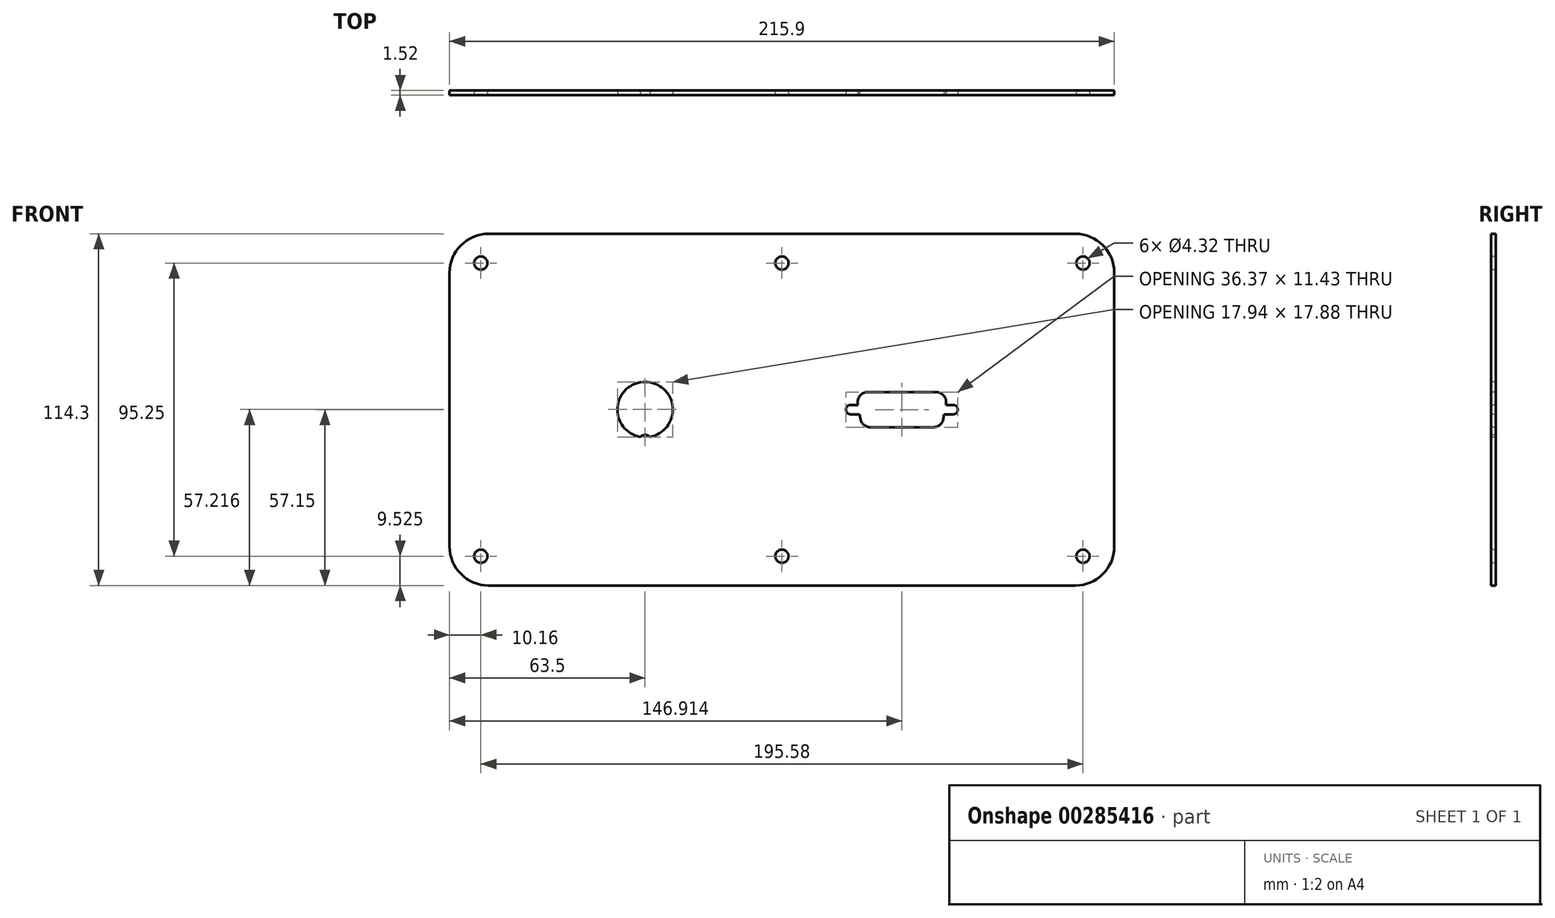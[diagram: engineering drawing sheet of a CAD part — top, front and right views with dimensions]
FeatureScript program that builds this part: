
annotation { "Feature Type Name" : "Feature", "Feature Type Description" : "" }
export const myFeature = defineFeature(function(context is Context, id is Id, definition is map)
    precondition{}
    {
        {
            var Q0;
            Q0=qCreatedBy(makeId("Front.planeOp"),FACE);
            var sketch = newSketch(context, id + "F0", { "sketchPlane" : qUnion([Q0])});
            skLineSegment(sketch, "E0.bottom", {"start": v(33.27, -22.23) * mm, "end": v(182.63, -22.23) * mm, "construction": true});
            skLineSegment(sketch, "E0.top", {"start": v(33.27, -92.08) * mm, "end": v(182.63, -92.08) * mm, "construction": true});
            skLineSegment(sketch, "E0.left", {"start": v(24.13, -31.37) * mm, "end": v(24.13, -82.93) * mm, "construction": true});
            skLineSegment(sketch, "E0.right", {"start": v(191.77, -31.37) * mm, "end": v(191.77, -82.93) * mm, "construction": true});
            skPoint(sketch, "E1.visualSharp", {"position": v(24.13, -22.23) * mm});
            skArc(sketch, "E1.filletArc", {"start": v(33.27, -22.23) * mm, "mid": v(26.8, -24.9) * mm, "end": v(24.13, -31.37) * mm, "construction": true});
            skPoint(sketch, "E2.visualSharp", {"position": v(191.77, -22.23) * mm});
            skArc(sketch, "E2.filletArc", {"start": v(191.77, -31.37) * mm, "mid": v(189.1, -24.9) * mm, "end": v(182.63, -22.22) * mm, "construction": true});
            skPoint(sketch, "E3.visualSharp", {"position": v(191.77, -92.08) * mm});
            skArc(sketch, "E3.filletArc", {"start": v(182.63, -92.08) * mm, "mid": v(189.1, -89.4) * mm, "end": v(191.77, -82.93) * mm, "construction": true});
            skPoint(sketch, "E4.visualSharp", {"position": v(24.13, -92.08) * mm});
            skArc(sketch, "E4.filletArc", {"start": v(24.13, -82.93) * mm, "mid": v(26.8, -89.4) * mm, "end": v(33.27, -92.07) * mm, "construction": true});
            skLineSegment(sketch, "E5.bottom", {"start": v(12.7, 0) * mm, "end": v(203.2, 0) * mm});
            skLineSegment(sketch, "E5.top", {"start": v(12.7, -114.3) * mm, "end": v(203.2, -114.3) * mm});
            skLineSegment(sketch, "E5.left", {"start": v(0, -12.7) * mm, "end": v(0, -101.6) * mm});
            skLineSegment(sketch, "E5.right", {"start": v(215.9, -12.7) * mm, "end": v(215.9, -101.6) * mm});
            skPoint(sketch, "E6.visualSharp", {"position": v(0, 0) * mm});
            skArc(sketch, "E6.filletArc", {"start": v(12.7, 0) * mm, "mid": v(3.72, -3.72) * mm, "end": v(0, -12.7) * mm});
            skPoint(sketch, "E7.visualSharp", {"position": v(215.9, 0) * mm});
            skArc(sketch, "E7.filletArc", {"start": v(215.9, -12.7) * mm, "mid": v(212.18, -3.72) * mm, "end": v(203.2, 0) * mm});
            skPoint(sketch, "E8.visualSharp", {"position": v(215.9, -114.3) * mm});
            skArc(sketch, "E8.filletArc", {"start": v(203.2, -114.3) * mm, "mid": v(212.18, -110.58) * mm, "end": v(215.9, -101.6) * mm});
            skPoint(sketch, "E9.visualSharp", {"position": v(0, -114.3) * mm});
            skArc(sketch, "E9.filletArc", {"start": v(0, -101.6) * mm, "mid": v(3.72, -110.58) * mm, "end": v(12.7, -114.3) * mm});
            skLineSegment(sketch, "E10", {"start": v(107.95, 0) * mm, "end": v(107.95, -114.3) * mm, "construction": true});
            skLineSegment(sketch, "E11", {"start": v(0, -57.15) * mm, "end": v(215.9, -57.15) * mm, "construction": true});
            skPoint(sketch, "E12", {"position": v(107.95, -22.23) * mm});
            skPoint(sketch, "E13", {"position": v(191.77, -57.15) * mm});
            skPoint(sketch, "E14", {"position": v(10.16, -9.52) * mm});
            skPoint(sketch, "E15", {"position": v(107.95, -9.52) * mm});
            skPoint(sketch, "E16", {"position": v(205.74, -9.52) * mm});
            skPoint(sketch, "E17", {"position": v(205.74, -104.78) * mm});
            skPoint(sketch, "E18", {"position": v(107.95, -104.78) * mm});
            skPoint(sketch, "E19", {"position": v(10.16, -104.78) * mm});
            skLineSegment(sketch, "E20", {"start": v(10.16, -9.52) * mm, "end": v(10.16, -104.78) * mm, "construction": true});
            skSolve(sketch);
        }
        {
            var Q0;
            Q0=makeQuery(id+"F0.imprint","IMPRINT",FACE,{"disambiguationData":[TD([[makeQuery(id+"F0.imprint","IMPRINT",EDGE,{"derivedFrom":sQuery(id+"F0.wireOp",EDGE,"E5.bottom")}),-1.0]])]});
            extrude(context, id + "F1", {"entities" : qUnion([Q0]), "depth" : 1.52 * mm});
        }
        {
            var Q0;
            Q0=makeQuery(id+"F1.opExtrude","CAP_FACE",FACE,{"disambiguationData":[OSD([sQuery(id+"F0.wireOp",EDGE,"E5.bottom"),sQuery(id+"F0.wireOp",EDGE,"E5.top"),sQuery(id+"F0.wireOp",EDGE,"E5.left"),sQuery(id+"F0.wireOp",EDGE,"E5.right"),sQuery(id+"F0.wireOp",EDGE,"E6.filletArc"),sQuery(id+"F0.wireOp",EDGE,"E7.filletArc"),sQuery(id+"F0.wireOp",EDGE,"E8.filletArc"),sQuery(id+"F0.wireOp",EDGE,"E9.filletArc")])],"isStart":false});
            var sketch = newSketch(context, id + "F2", { "sketchPlane" : qUnion([Q0])});
            skArc(sketch, "E21", {"start": v(65.04, -66.02) * mm, "mid": v(63.5, -48.15) * mm, "end": v(61.96, -66.02) * mm});
            skArc(sketch, "E22", {"start": v(65.04, -66.02) * mm, "mid": v(63.5, -65.35) * mm, "end": v(61.96, -66.02) * mm});
            skLineSegment(sketch, "E23", {"start": v(63.5, -57.15) * mm, "end": v(63.5, -65.35) * mm, "construction": true});
            skLineSegment(sketch, "E24", {"start": v(0, -57.15) * mm, "end": v(215.9, -57.15) * mm, "construction": true});
            skLineSegment(sketch, "E25.bottom", {"start": v(163.58, -51.44) * mm, "end": v(130.25, -51.44) * mm, "construction": true});
            skLineSegment(sketch, "E25.top", {"start": v(163.58, -62.87) * mm, "end": v(130.25, -62.87) * mm, "construction": true});
            skLineSegment(sketch, "E25.left", {"start": v(163.58, -51.44) * mm, "end": v(163.58, -62.87) * mm, "construction": true});
            skLineSegment(sketch, "E25.right", {"start": v(130.25, -51.44) * mm, "end": v(130.25, -62.87) * mm, "construction": true});
            skLineSegment(sketch, "E26", {"start": v(160.39, -60.14) * mm, "end": v(160.65, -58.67) * mm});
            skLineSegment(sketch, "E27", {"start": v(133.44, -60.14) * mm, "end": v(133.18, -58.67) * mm});
            skLineSegment(sketch, "E28", {"start": v(146.91, -62.87) * mm, "end": v(146.91, -51.44) * mm, "construction": true});
            skArc(sketch, "E29", {"start": v(163.58, -58.67) * mm, "mid": v(165.1, -57.15) * mm, "end": v(163.58, -55.63) * mm});
            skArc(sketch, "E30", {"start": v(130.25, -55.63) * mm, "mid": v(128.73, -57.15) * mm, "end": v(130.25, -58.67) * mm});
            skLineSegment(sketch, "E31", {"start": v(163.58, -57.15) * mm, "end": v(130.25, -57.15) * mm, "construction": true});
            skLineSegment(sketch, "E32", {"start": v(157.14, -62.87) * mm, "end": v(136.7, -62.87) * mm});
            skLineSegment(sketch, "E33", {"start": v(135.84, -51.44) * mm, "end": v(157.99, -51.44) * mm});
            skPoint(sketch, "E34.visualSharp", {"position": v(159.9, -62.87) * mm});
            skArc(sketch, "E34.filletArc", {"start": v(157.14, -62.87) * mm, "mid": v(159.26, -62.1) * mm, "end": v(160.39, -60.14) * mm});
            skPoint(sketch, "E35.visualSharp", {"position": v(133.92, -62.87) * mm});
            skArc(sketch, "E35.filletArc", {"start": v(133.44, -60.14) * mm, "mid": v(134.57, -62.1) * mm, "end": v(136.7, -62.87) * mm});
            skPoint(sketch, "E36.visualSharp", {"position": v(131.9, -51.44) * mm});
            skArc(sketch, "E36.filletArc", {"start": v(135.84, -51.44) * mm, "mid": v(133.3, -52.61) * mm, "end": v(132.59, -55.31) * mm});
            skPoint(sketch, "E37.visualSharp", {"position": v(161.92, -51.44) * mm});
            skArc(sketch, "E37.filletArc", {"start": v(161.24, -55.31) * mm, "mid": v(160.52, -52.61) * mm, "end": v(157.99, -51.44) * mm});
            skLineSegment(sketch, "E38", {"start": v(163.58, -58.67) * mm, "end": v(160.65, -58.67) * mm});
            skLineSegment(sketch, "E39", {"start": v(163.58, -55.63) * mm, "end": v(161.18, -55.63) * mm});
            skLineSegment(sketch, "E40", {"start": v(130.25, -58.67) * mm, "end": v(133.18, -58.67) * mm});
            skLineSegment(sketch, "E41", {"start": v(130.25, -55.63) * mm, "end": v(132.64, -55.63) * mm});
            skLineSegment(sketch, "E42.trimOffspring", {"start": v(132.64, -55.63) * mm, "end": v(132.59, -55.31) * mm});
            skLineSegment(sketch, "E43.trimOffspring", {"start": v(161.18, -55.63) * mm, "end": v(161.24, -55.31) * mm});
            skSolve(sketch);
        }
        {
            var Q0;
            Q0 = qSketchRegion(id + "F2", true);
            extrude(context, id + "F3", {"entities" : qUnion([Q0]), "operationType" : NewBodyOperationType.REMOVE, "endBound" : BoundingType.THROUGH_ALL, "oppositeDirection" : true, "depth" : 25.4 * mm});
        }
        {
            var Q0;
            {var subQ0=sQuery(id+"F0.wireOp",EDGE,"E9.filletArc");var subQ1=sQuery(id+"F0.wireOp",EDGE,"E8.filletArc");var subQ2=sQuery(id+"F0.wireOp",EDGE,"E5.left");var subQ3=sQuery(id+"F0.wireOp",EDGE,"E5.top");var subQ4=sQuery(id+"F0.wireOp",EDGE,"E5.right");var subQ5=sQuery(id+"F0.wireOp",EDGE,"E6.filletArc");var subQ6=sQuery(id+"F0.wireOp",EDGE,"E5.bottom");var subQ7=sQuery(id+"F0.wireOp",EDGE,"E7.filletArc");Q0=makeQuery(id+"FZWJOkOxSF8nC3A_1.boolean.opBoolean","SPLIT",FACE,{"disambiguationData":[TD([makeQuery(id+"F1.opExtrude","SWEPT_FACE",FACE,{"disambiguationData":[OSD([subQ6])]})])],"derivedFrom":makeQuery(id+"F1.opExtrude","CAP_FACE",FACE,{"disambiguationData":[OSD([subQ6,subQ3,subQ2,subQ4,subQ5,subQ7,subQ1,subQ0])],"isStart":false})});}
            var sketch = newSketch(context, id + "F4", { "sketchPlane" : qUnion([Q0])});
            skPoint(sketch, "E44", {"position": v(10.16, -9.52) * mm});
            skPoint(sketch, "E45", {"position": v(107.95, -9.52) * mm});
            skPoint(sketch, "E46", {"position": v(205.74, -9.52) * mm});
            skPoint(sketch, "E47", {"position": v(205.74, -104.78) * mm});
            skPoint(sketch, "E48", {"position": v(107.95, -104.78) * mm});
            skPoint(sketch, "E49", {"position": v(10.16, -104.78) * mm});
            skSolve(sketch);
        }
        {
            var Q0;
            Q0=sQuery(id+"F4.wireOp",VERTEX,"E44");
            var Q1;
            Q1=sQuery(id+"F4.wireOp",VERTEX,"E45");
            var Q2;
            Q2=sQuery(id+"F4.wireOp",VERTEX,"E46");
            var Q3;
            Q3=sQuery(id+"F4.wireOp",VERTEX,"E47");
            var Q4;
            Q4=sQuery(id+"F4.wireOp",VERTEX,"E48");
            var Q5;
            Q5=sQuery(id+"F4.wireOp",VERTEX,"E49");
            var Q6;
            Q6=makeQuery(id+"F1.opExtrude","SWEPT_BODY",BODY,{"disambiguationData":[OSD([sQuery(id+"F0.wireOp",EDGE,"E5.bottom"),sQuery(id+"F0.wireOp",EDGE,"E5.top"),sQuery(id+"F0.wireOp",EDGE,"E5.left"),sQuery(id+"F0.wireOp",EDGE,"E5.right"),sQuery(id+"F0.wireOp",EDGE,"E6.filletArc"),sQuery(id+"F0.wireOp",EDGE,"E7.filletArc"),sQuery(id+"F0.wireOp",EDGE,"E8.filletArc"),sQuery(id+"F0.wireOp",EDGE,"E9.filletArc")])]});
            hole(context, id + "F5", {"style" : HoleStyle.SIMPLE, "endStyle" : HoleEndStyle.THROUGH, "standardTappedOrClearance" : lookupTablePath({ "standard" : "ANSI", "fit" : "Close", "size" : "#8", "type" : "Clearance" }), "standardBlindInLast" : lookupTablePath({ "fit" : "Close", "standard" : "ANSI", "size" : "#8", "type" : "Clearance" }), "holeDiameter" : 4.32 * mm, "isTappedThrough" : true, "tappedDepth" : 2.4 * mm, "tapClearance" : 3, "startFromSketch" : true, "locations" : qUnion([Q0, Q1, Q2, Q3, Q4, Q5]), "scope" : qUnion([Q6])});
        }
    });
